# Revit family: RAINIER FINS 1.5in - 36 X 36
name_source: partatom
category: Generic Models
units: mm (PartAtom-declared; Revit-internal decimal feet)

## family parameters
Can host rebar = No
Cut with Voids When Loaded = No
Host = Face
Maintain Annotation Orientation = No
Part Type = Normal
Room Calculation Point = No
Round Connector Dimension = Use Diameter
Shared = No

## types (36) — shared parameters
Default Elevation = 4' - 0"

## per-type parameters (varying)
| type | FELT MATERIAL | WOOD MATERIAL |
| STONE FELT - 1" OAK WOOD | Cambio Felt Board - Stone | Oak - Clear |
| STONE FELT - 1" UMBER WOOD | Cambio Felt Board - Stone | Umber |
| STONE FELT - 1" LEATHER WOOD | Cambio Felt Board - Stone | Leather |
| STONE FELT - 1" EBONY WOOD | Cambio Felt Board - Stone | Ebony |
| SAND DOLLAR FELT - EBONY WOOD | Cambio Felt Board - Sand Dollar | Ebony |
| SAND DOLLAR FELT - 1" LEATHER WOOD | Cambio Felt Board - Sand Dollar | Leather |
| SAND DOLLAR FELT - 1" UMBER WOOD | Cambio Felt Board - Sand Dollar | Umber |
| SAND DOLLAR FELT - 1" CLEAR OAK WOOD | Cambio Felt Board - Sand Dollar | Oak - Clear |
| PEPPER FELT - 1" CLEAR OAK WOOD | Cambio Felt Board - Pepper | Oak - Clear |
| PEPPER FELT - 1" UMBER WOOD | Cambio Felt Board - Pepper | Umber |
| PEPPER FELT - 1" LEATHER WOOD | Cambio Felt Board - Pepper | Leather |
| PEPPER FELT - 1" EBONY WOOD | Cambio Felt Board - Pepper | Ebony |
| OAT FELT - 1" EBONY WOOD | Cambio Felt Board - Oat | Ebony |
| OAT FELT - 1" LEATHER WOOD | Cambio Felt Board - Oat | Leather |
| OAT FELT - 1" UMBER WOOD | Cambio Felt Board - Oat | Umber |
| OAT FELT - 1" CLEAR OAK WOOD | Cambio Felt Board - Oat | Oak - Clear |
| MARBLE FELT - 1" CLEAR OAK WOOD | Cambio Felt Board - Marble | Oak - Clear |
| MARBLE FELT - 1" UMBER WOOD | Cambio Felt Board - Marble | Umber |
| MARBLE FELT - 1" LEATHER WOOD | Cambio Felt Board - Marble | Leather |
| MARBLE FELT - 1" EBONY WOOD | Cambio Felt Board - Marble | Ebony |
| GREY FELT - 1" CLEAR OAK WOOD | Cambio Felt Board - Grey | Oak - Clear |
| GREY  FELT - 1" UMBER WOOD | Cambio Felt Board - Grey | Umber |
| GREY  FELT - 1" LEATHER WOOD | Cambio Felt Board - Grey | Leather |
| GREY  FELT - 1" EBONY WOOD | Cambio Felt Board - Grey | Ebony |
| EARTH BROWN  FELT - 1" EBONY WOOD | Cambio Felt Board - Earth Brown | Ebony |
| EARTH BROWN  FELT - 1" LEATHER WOOD | Cambio Felt Board - Earth Brown | Leather |
| EARTH BROWN  FELT - 1" UMBER WOOD | Cambio Felt Board - Earth Brown | Umber |
| EARTH BROWN  FELT - 1" CLEAR OAK WOOD | Cambio Felt Board - Earth Brown | Oak - Clear |
| CHARCOAL  FELT - 1" CLEAR OAK WOOD | Cambio Felt Board - Charcoal | Oak - Clear |
| CHARCOAL  FELT - 1" UMBER WOOD | Cambio Felt Board - Charcoal | Umber |
| CHARCOAL  FELT - 1" LEATHER WOOD | Cambio Felt Board - Charcoal | Leather |
| CHARCOAL  FELT - 1" EBONY WOOD | Cambio Felt Board - Charcoal | Ebony |
| BLACK  FELT - 1" LEATHER WOOD | Cambio Felt Board - Black | Leather |
| BLACK  FELT - 1" EBONY WOOD | Cambio Felt Board - Black | Ebony |
| BLACK  FELT - 1" UMBER WOOD | Cambio Felt Board - Black | Umber |
| BLACK  FELT - 1" CLEAR OAK WOOD | Cambio Felt Board - Black | Oak - Clear |

## geometry (parser evidence)
native form markers: Sweep x8
no freeform markers — native parametric forms only
